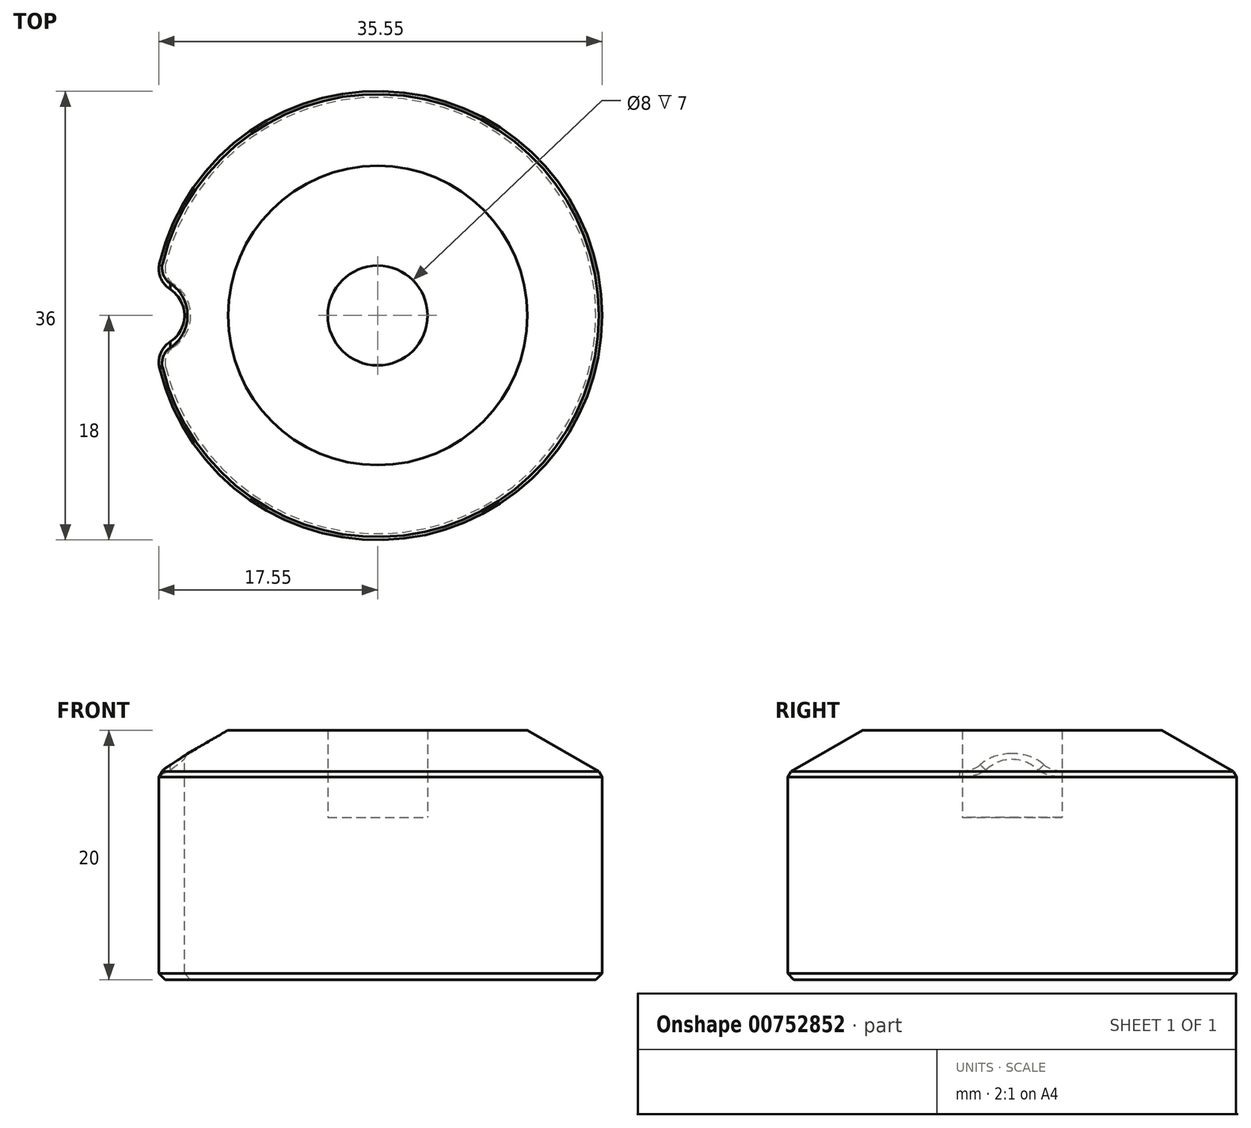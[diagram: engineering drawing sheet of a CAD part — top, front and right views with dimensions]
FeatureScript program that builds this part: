
annotation { "Feature Type Name" : "Feature", "Feature Type Description" : "" }
export const myFeature = defineFeature(function(context is Context, id is Id, definition is map)
    precondition{}
    {
        {
            var Q0;
            Q0=qCreatedBy(makeId("Front.planeOp"),FACE);
            var sketch = newSketch(context, id + "F0", { "sketchPlane" : qUnion([Q0])});
            skLineSegment(sketch, "E0", {"start": v(0, 0) * mm, "end": v(-4, 0) * mm});
            skLineSegment(sketch, "E1", {"start": v(-4, 0) * mm, "end": v(-4, 7) * mm});
            skLineSegment(sketch, "E2", {"start": v(-4, 7) * mm, "end": v(-12, 7) * mm});
            skLineSegment(sketch, "E3", {"start": v(-12, 7) * mm, "end": v(-18, 3.54) * mm});
            skLineSegment(sketch, "E4", {"start": v(-18, 3.54) * mm, "end": v(-18, -13) * mm});
            skLineSegment(sketch, "E5", {"start": v(-18, -13) * mm, "end": v(0, -13) * mm});
            skLineSegment(sketch, "E6", {"start": v(0, -13) * mm, "end": v(0, 0) * mm});
            skSolve(sketch);
        }
        {
            var Q0;
            Q0=makeQuery(id+"F0.imprint","IMPRINT",FACE,{"disambiguationData":[TD([[makeQuery(id+"F0.imprint","IMPRINT",EDGE,{"derivedFrom":sQuery(id+"F0.wireOp",EDGE,"E0")}),1.0]])]});
            var Q1;
            Q1=sQuery(id+"F0.wireOp",EDGE,"E6");
            revolve(context, id + "F1", {"surfaceOperationType" : NewSurfaceOperationType.NEW, "entities" : qUnion([Q0]), "axis" : qUnion([Q1]), "revolveType" : RevolveType.FULL});
        }
        {
            var Q0;
            Q0=qCreatedBy(makeId("Top.planeOp"),FACE);
            var sketch = newSketch(context, id + "F2", { "sketchPlane" : qUnion([Q0])});
            skCircle(sketch, "E7", {"center": v(-18, 0) * mm, "radius": 2.5 * mm});
            skSolve(sketch);
        }
        {
            var Q0;
            Q0=makeQuery(id+"F2.imprint","IMPRINT",FACE,{"disambiguationData":[TD([[makeQuery(id+"F2.imprint","IMPRINT",EDGE,{"derivedFrom":sQuery(id+"F2.wireOp",EDGE,"E7")}),1.0]])]});
            extrude(context, id + "F3", {"entities" : qUnion([Q0]), "operationType" : NewBodyOperationType.REMOVE, "oppositeDirection" : true, "depth" : 25 * mm, "offsetDistance" : 25 * mm, "hasSecondDirection" : true, "secondDirectionOppositeDirection" : false, "secondDirectionDepth" : 25 * mm});
        }
        {
            var Q0;
            Q0=makeQuery(id+"F3.boolean.opBoolean","INTERSECT",EDGE,{"disambiguationData":[OD(1.0)],"derivedFrom":[makeQuery(id+"F1.opRevolve","SWEPT_FACE",FACE,{"disambiguationData":[OSD([sQuery(id+"F0.wireOp",EDGE,"E4")])]}),makeQuery(id+"F3.opExtrude","SWEPT_FACE",FACE,{"disambiguationData":[OSD([sQuery(id+"F2.wireOp",EDGE,"E7")])]})]});
            var Q1;
            Q1=makeQuery(id+"F3.boolean.opBoolean","INTERSECT",EDGE,{"disambiguationData":[OD(0.0)],"derivedFrom":[makeQuery(id+"F1.opRevolve","SWEPT_FACE",FACE,{"disambiguationData":[OSD([sQuery(id+"F0.wireOp",EDGE,"E4")])]}),makeQuery(id+"F3.opExtrude","SWEPT_FACE",FACE,{"disambiguationData":[OSD([sQuery(id+"F2.wireOp",EDGE,"E7")])]})]});
            fillet(context, id + "F4", {"entities" : qUnion([Q0, Q1]), "radius" : 2 * mm, "tangentPropagation" : true, "allowEdgeOverflow" : false});
        }
        {
            var Q0;
            {var subQ0=sQuery(id+"F0.wireOp",EDGE,"E3");var subQ2=sQuery(id+"F0.wireOp",EDGE,"E4");var subQ3=makeQuery(id+"F1.opRevolve","SWEPT_FACE",FACE,{"disambiguationData":[OSD([subQ2])]});var subQ4=sQuery(id+"F2.wireOp",EDGE,"E7");var subQ5=makeQuery(id+"Fhnu2t5l6bls0jl_1.2.F3.opExtrude","SWEPT_FACE",FACE,{"disambiguationData":[OSD([subQ4])]});var subQ6=makeQuery(id+"F4.opFillet","BLEND_FACE",FACE,{"disambiguationData":[OSD([subQ2,subQ4]),TDD([makeQuery(id+"F3.boolean.opBoolean","INTERSECT",EDGE,{"disambiguationData":[OD(1.0)],"derivedFrom":[subQ3,makeQuery(id+"F3.opExtrude","SWEPT_FACE",FACE,{"disambiguationData":[OSD([subQ4])]})]})])]});Q0=makeQuery(id+"Fhnu2t5l6bls0jl_1.3.F3.boolean.opBoolean","SPLIT",EDGE,{"disambiguationData":[TD([makeQuery(id+"Fhnu2t5l6bls0jl_1.2.F4.opFillet","BLEND_FACE",FACE,{"disambiguationData":[OSD([subQ2,subQ4]),TDD([makeQuery(id+"Fhnu2t5l6bls0jl_1.2.F3.boolean.opBoolean","INTERSECT",EDGE,{"disambiguationData":[OD(0.0)],"derivedFrom":[makeQuery(id+"Fhnu2t5l6bls0jl_1.1.F3.boolean.opBoolean","SPLIT",FACE,{"disambiguationData":[TD([subQ6])],"derivedFrom":subQ3}),subQ5]})])]})])],"derivedFrom":makeQuery(id+"Fhnu2t5l6bls0jl_1.2.F3.boolean.opBoolean","SPLIT",EDGE,{"disambiguationData":[TD([subQ6])],"derivedFrom":makeQuery(id+"Fhnu2t5l6bls0jl_1.1.F3.boolean.opBoolean","SPLIT",EDGE,{"disambiguationData":[TD([subQ6])],"derivedFrom":makeQuery(id+"F1.opRevolve","SWEPT_EDGE",EDGE,{"disambiguationData":[OSD([subQ0,subQ2])]})})})});}
            var Q1;
            {var subQ0=sQuery(id+"F0.wireOp",EDGE,"E4");var subQ1=makeQuery(id+"F1.opRevolve","SWEPT_FACE",FACE,{"disambiguationData":[OSD([subQ0])]});var subQ2=sQuery(id+"F0.wireOp",EDGE,"E5");var subQ4=sQuery(id+"F2.wireOp",EDGE,"E7");var subQ5=makeQuery(id+"Fhnu2t5l6bls0jl_1.2.F3.opExtrude","SWEPT_FACE",FACE,{"disambiguationData":[OSD([subQ4])]});var subQ6=makeQuery(id+"F4.opFillet","BLEND_FACE",FACE,{"disambiguationData":[OSD([subQ0,subQ4]),TDD([makeQuery(id+"F3.boolean.opBoolean","INTERSECT",EDGE,{"disambiguationData":[OD(1.0)],"derivedFrom":[subQ1,makeQuery(id+"F3.opExtrude","SWEPT_FACE",FACE,{"disambiguationData":[OSD([subQ4])]})]})])]});Q1=makeQuery(id+"Fhnu2t5l6bls0jl_1.3.F3.boolean.opBoolean","SPLIT",EDGE,{"disambiguationData":[TD([makeQuery(id+"Fhnu2t5l6bls0jl_1.2.F4.opFillet","BLEND_FACE",FACE,{"disambiguationData":[OSD([subQ0,subQ4]),TDD([makeQuery(id+"Fhnu2t5l6bls0jl_1.2.F3.boolean.opBoolean","INTERSECT",EDGE,{"disambiguationData":[OD(0.0)],"derivedFrom":[makeQuery(id+"Fhnu2t5l6bls0jl_1.1.F3.boolean.opBoolean","SPLIT",FACE,{"disambiguationData":[TD([subQ6])],"derivedFrom":subQ1}),subQ5]})])]})])],"derivedFrom":makeQuery(id+"Fhnu2t5l6bls0jl_1.2.F3.boolean.opBoolean","SPLIT",EDGE,{"disambiguationData":[TD([subQ6])],"derivedFrom":makeQuery(id+"Fhnu2t5l6bls0jl_1.1.F3.boolean.opBoolean","SPLIT",EDGE,{"disambiguationData":[TD([subQ6])],"derivedFrom":makeQuery(id+"F1.opRevolve","SWEPT_EDGE",EDGE,{"disambiguationData":[OSD([subQ0,subQ2])]})})})});}
            chamfer(context, id + "F5", {"entities" : qUnion([Q0, Q1]), "width" : .5 * mm, "tangentPropagation" : true});
        }
    });
